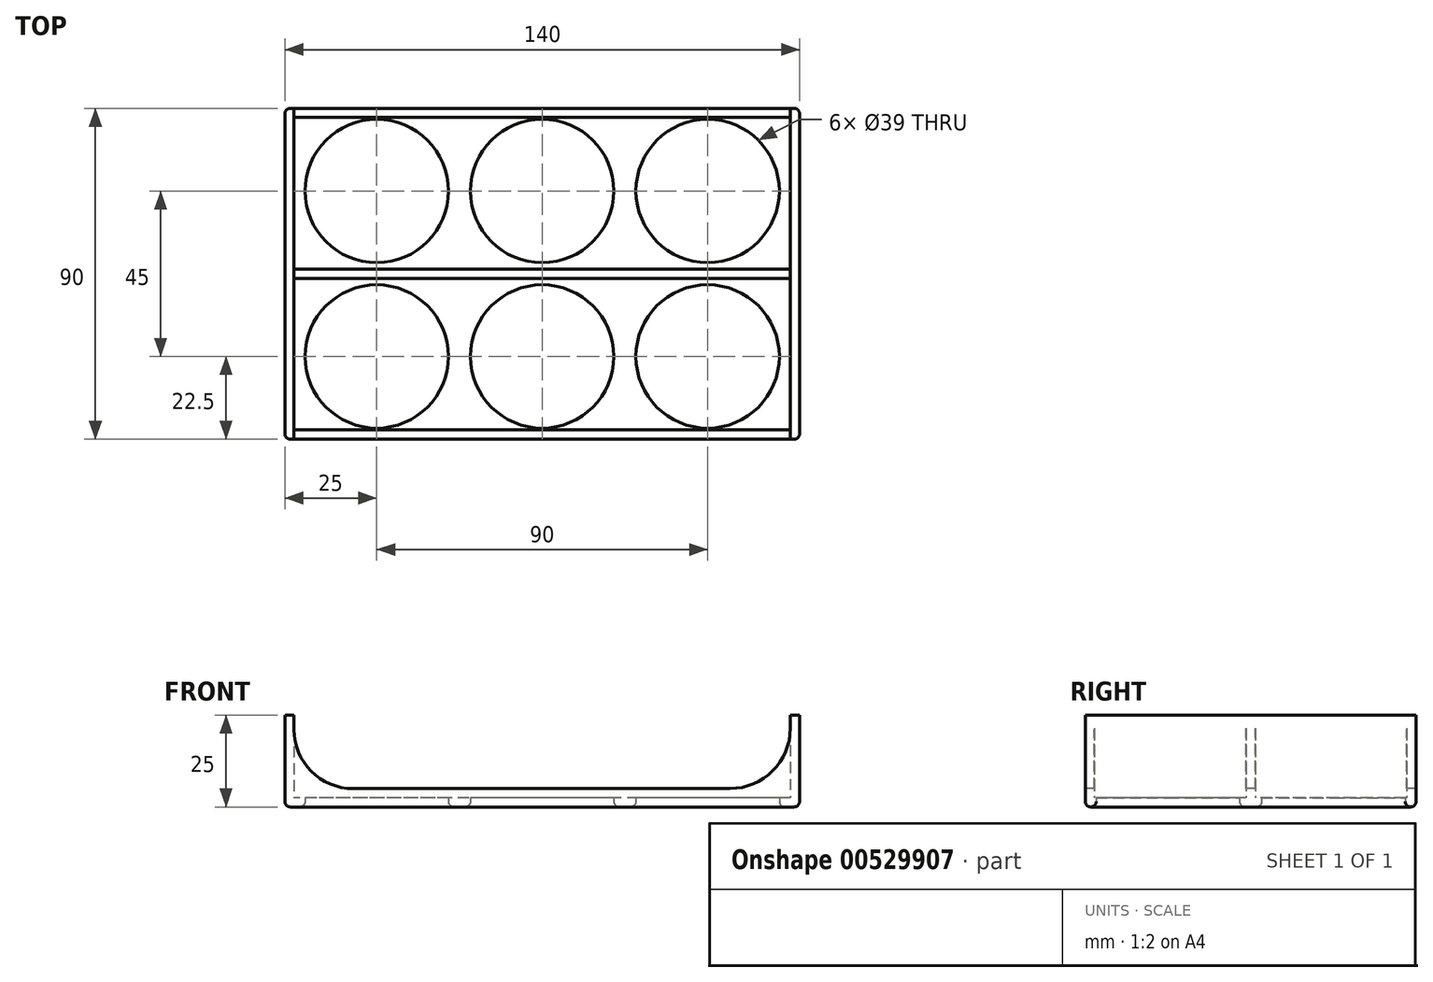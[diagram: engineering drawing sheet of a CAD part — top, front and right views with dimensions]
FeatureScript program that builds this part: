
annotation { "Feature Type Name" : "Feature", "Feature Type Description" : "" }
export const myFeature = defineFeature(function(context is Context, id is Id, definition is map)
    precondition{}
    {
        {
            var Q0;
            Q0=qCreatedBy(makeId("Top.planeOp"),FACE);
            var sketch = newSketch(context, id + "F0", { "sketchPlane" : qUnion([Q0])});
            skLineSegment(sketch, "E0.bottom", {"start": v(-140, 45) * mm, "end": v(0, 45) * mm});
            skLineSegment(sketch, "E0.top", {"start": v(-140, -45) * mm, "end": v(0, -45) * mm});
            skLineSegment(sketch, "E0.left", {"start": v(-140, 45) * mm, "end": v(-140, -45) * mm});
            skLineSegment(sketch, "E0.right", {"start": v(0, 45) * mm, "end": v(0, -45) * mm});
            skSolve(sketch);
        }
        {
            var Q0;
            Q0=makeQuery(id+"F0.imprint","IMPRINT",FACE,{"disambiguationData":[TD([[makeQuery(id+"F0.imprint","IMPRINT",EDGE,{"derivedFrom":sQuery(id+"F0.wireOp",EDGE,"E0.bottom")}),-1.0]])]});
            extrude(context, id + "F1", {"entities" : qUnion([Q0]), "depth" : 25 * mm, "offsetDistance" : 25 * mm});
        }
        {
            var Q0;
            Q0=makeQuery(id+"F1.opExtrude","CAP_FACE",FACE,{"disambiguationData":[OSD([sQuery(id+"F0.wireOp",EDGE,"E0.bottom"),sQuery(id+"F0.wireOp",EDGE,"E0.top"),sQuery(id+"F0.wireOp",EDGE,"E0.left"),sQuery(id+"F0.wireOp",EDGE,"E0.right")])],"isStart":false});
            shell(context, id + "F2", {"entities" : qUnion([Q0]), "thickness" : 2.5 * mm});
        }
        {
            var Q0;
            Q0=makeQuery(id+"F1.opExtrude","SWEPT_FACE",FACE,{"disambiguationData":[OSD([sQuery(id+"F0.wireOp",EDGE,"E0.top")])]});
            var sketch = newSketch(context, id + "F3", { "sketchPlane" : qUnion([Q0])});
            skLineSegment(sketch, "E1.bottom", {"start": v(-137.5, 25) * mm, "end": v(-2.5, 25) * mm});
            skLineSegment(sketch, "E1.left", {"start": v(-137.5, 25) * mm, "end": v(-137.5, 21.07) * mm});
            skLineSegment(sketch, "E1.right", {"start": v(-2.5, 25) * mm, "end": v(-2.5, 21.43) * mm});
            skArc(sketch, "E2", {"start": v(-137.5, 21.07) * mm, "mid": v(-132.8, 9.7) * mm, "end": v(-121.43, 5) * mm});
            skLineSegment(sketch, "E3", {"start": v(-121.43, 5) * mm, "end": v(-18.93, 5) * mm});
            skArc(sketch, "E4", {"start": v(-18.93, 5) * mm, "mid": v(-7.31, 9.81) * mm, "end": v(-2.5, 21.43) * mm});
            skSolve(sketch);
        }
        {
            var Q0;
            Q0=makeQuery(id+"F1.opExtrude","CAP_FACE",FACE,{"disambiguationData":[OSD([sQuery(id+"F0.wireOp",EDGE,"E0.bottom"),sQuery(id+"F0.wireOp",EDGE,"E0.top"),sQuery(id+"F0.wireOp",EDGE,"E0.left"),sQuery(id+"F0.wireOp",EDGE,"E0.right")])],"isStart":true});
            var sketch = newSketch(context, id + "F4", { "sketchPlane" : qUnion([Q0])});
            skCircle(sketch, "E5", {"center": v(-25, 22.5) * mm, "radius": 19.5 * mm});
            skCircle(sketch, "E6.1.0.0", {"center": v(-70, 22.5) * mm, "radius": 19.5 * mm});
            skCircle(sketch, "E6.2.0.0", {"center": v(-115, 22.5) * mm, "radius": 19.5 * mm});
            skLineSegment(sketch, "E6.direction1", {"start": v(-25, 22.5) * mm, "end": v(-70, 22.5) * mm, "construction": true});
            skCircle(sketch, "E7.0.1.0", {"center": v(-70, -22.5) * mm, "radius": 19.5 * mm});
            skCircle(sketch, "E7.0.1.1", {"center": v(-115, -22.5) * mm, "radius": 19.5 * mm});
            skCircle(sketch, "E7.0.1.2", {"center": v(-25, -22.5) * mm, "radius": 19.5 * mm});
            skLineSegment(sketch, "E7.direction1", {"start": v(-115, 22.5) * mm, "end": v(-90, 22.5) * mm, "construction": true});
            skLineSegment(sketch, "E7.direction2", {"start": v(-115, 22.5) * mm, "end": v(-115, -22.5) * mm, "construction": true});
            skSolve(sketch);
        }
        {
            var Q0;
            Q0=makeQuery(id+"F4.imprint","IMPRINT",FACE,{"disambiguationData":[TD([[makeQuery(id+"F4.imprint","IMPRINT",EDGE,{"derivedFrom":sQuery(id+"F4.wireOp",EDGE,"E5")}),-1.0]])]});
            extrude(context, id + "F5", {"entities" : qUnion([Q0]), "operationType" : NewBodyOperationType.INTERSECT, "oppositeDirection" : true, "depth" : 25 * mm, "offsetDistance" : 25 * mm});
        }
        {
            var Q0;
            Q0=makeQuery(id+"F1.opExtrude","CAP_EDGE",EDGE,{"disambiguationData":[OSD([sQuery(id+"F0.wireOp",EDGE,"E0.top")])],"isStart":true});
            var Q1;
            Q1=makeQuery(id+"F1.opExtrude","CAP_EDGE",EDGE,{"disambiguationData":[OSD([sQuery(id+"F0.wireOp",EDGE,"E0.left")])],"isStart":true});
            var Q2;
            Q2=makeQuery(id+"F1.opExtrude","CAP_EDGE",EDGE,{"disambiguationData":[OSD([sQuery(id+"F0.wireOp",EDGE,"E0.bottom")])],"isStart":true});
            var Q3;
            Q3=makeQuery(id+"F1.opExtrude","CAP_EDGE",EDGE,{"disambiguationData":[OSD([sQuery(id+"F0.wireOp",EDGE,"E0.right")])],"isStart":true});
            var Q4;
            Q4=makeQuery(id+"F1.opExtrude","CAP_FACE",FACE,{"disambiguationData":[OSD([sQuery(id+"F0.wireOp",EDGE,"E0.bottom"),sQuery(id+"F0.wireOp",EDGE,"E0.top"),sQuery(id+"F0.wireOp",EDGE,"E0.left"),sQuery(id+"F0.wireOp",EDGE,"E0.right")])],"isStart":true});
            var Q5;
            Q5=makeQuery(id+"F1.opExtrude","SWEPT_EDGE",EDGE,{"disambiguationData":[OSD([sQuery(id+"F0.wireOp",EDGE,"E0.bottom"),sQuery(id+"F0.wireOp",EDGE,"E0.left")])]});
            var Q6;
            Q6=makeQuery(id+"F1.opExtrude","SWEPT_EDGE",EDGE,{"disambiguationData":[OSD([sQuery(id+"F0.wireOp",EDGE,"E0.top"),sQuery(id+"F0.wireOp",EDGE,"E0.left")])]});
            var Q7;
            Q7=makeQuery(id+"F1.opExtrude","SWEPT_EDGE",EDGE,{"disambiguationData":[OSD([sQuery(id+"F0.wireOp",EDGE,"E0.top"),sQuery(id+"F0.wireOp",EDGE,"E0.right")])]});
            var Q8;
            Q8=makeQuery(id+"F1.opExtrude","SWEPT_EDGE",EDGE,{"disambiguationData":[OSD([sQuery(id+"F0.wireOp",EDGE,"E0.bottom"),sQuery(id+"F0.wireOp",EDGE,"E0.right")])]});
            fillet(context, id + "F6", {"entities" : qUnion([Q0, Q1, Q2, Q3, Q4, Q5, Q6, Q7, Q8]), "radius" : 1.5 * mm, "tangentPropagation" : true, "allowEdgeOverflow" : false});
        }
        {
            var Q0;
            Q0=makeQuery(id+"F2.opShell","OFFSET_FACE",FACE,{"disambiguationData":[OSD([sQuery(id+"F0.wireOp",EDGE,"E0.bottom"),sQuery(id+"F0.wireOp",EDGE,"E0.top"),sQuery(id+"F0.wireOp",EDGE,"E0.left"),sQuery(id+"F0.wireOp",EDGE,"E0.right")])]});
            var sketch = newSketch(context, id + "F7", { "sketchPlane" : qUnion([Q0])});
            skPoint(sketch, "E8.firstSnap0", {"position": v(-2.5, 0) * mm});
            skLineSegment(sketch, "E8.top", {"start": v(-2.5, 1.25) * mm, "end": v(-137.5, 1.25) * mm});
            skLineSegment(sketch, "E8.left", {"start": v(-2.5, -1.25) * mm, "end": v(-2.5, 1.25) * mm});
            skLineSegment(sketch, "E8.right", {"start": v(-137.5, -1.25) * mm, "end": v(-137.5, 1.25) * mm});
            skLineSegment(sketch, "E9", {"start": v(-2.5, -1.25) * mm, "end": v(-137.5, -1.25) * mm});
            skSolve(sketch);
        }
        {
            var Q0;
            Q0=makeQuery(id+"F7.imprint","IMPRINT",FACE,{"disambiguationData":[TD([[makeQuery(id+"F7.imprint","IMPRINT",EDGE,{"derivedFrom":sQuery(id+"F7.wireOp",EDGE,"E8.top")}),1.0]])]});
            extrude(context, id + "F8", {"entities" : qUnion([Q0]), "operationType" : NewBodyOperationType.ADD, "depth" : 22.5 * mm, "offsetDistance" : 25 * mm});
        }
        {
            var Q0;
            Q0 = qSketchRegion(id + "F3", true);
            extrude(context, id + "F9", {"entities" : qUnion([Q0]), "operationType" : NewBodyOperationType.REMOVE, "endBound" : BoundingType.THROUGH_ALL, "oppositeDirection" : true, "depth" : 25 * mm, "offsetDistance" : 25 * mm});
        }
    });
